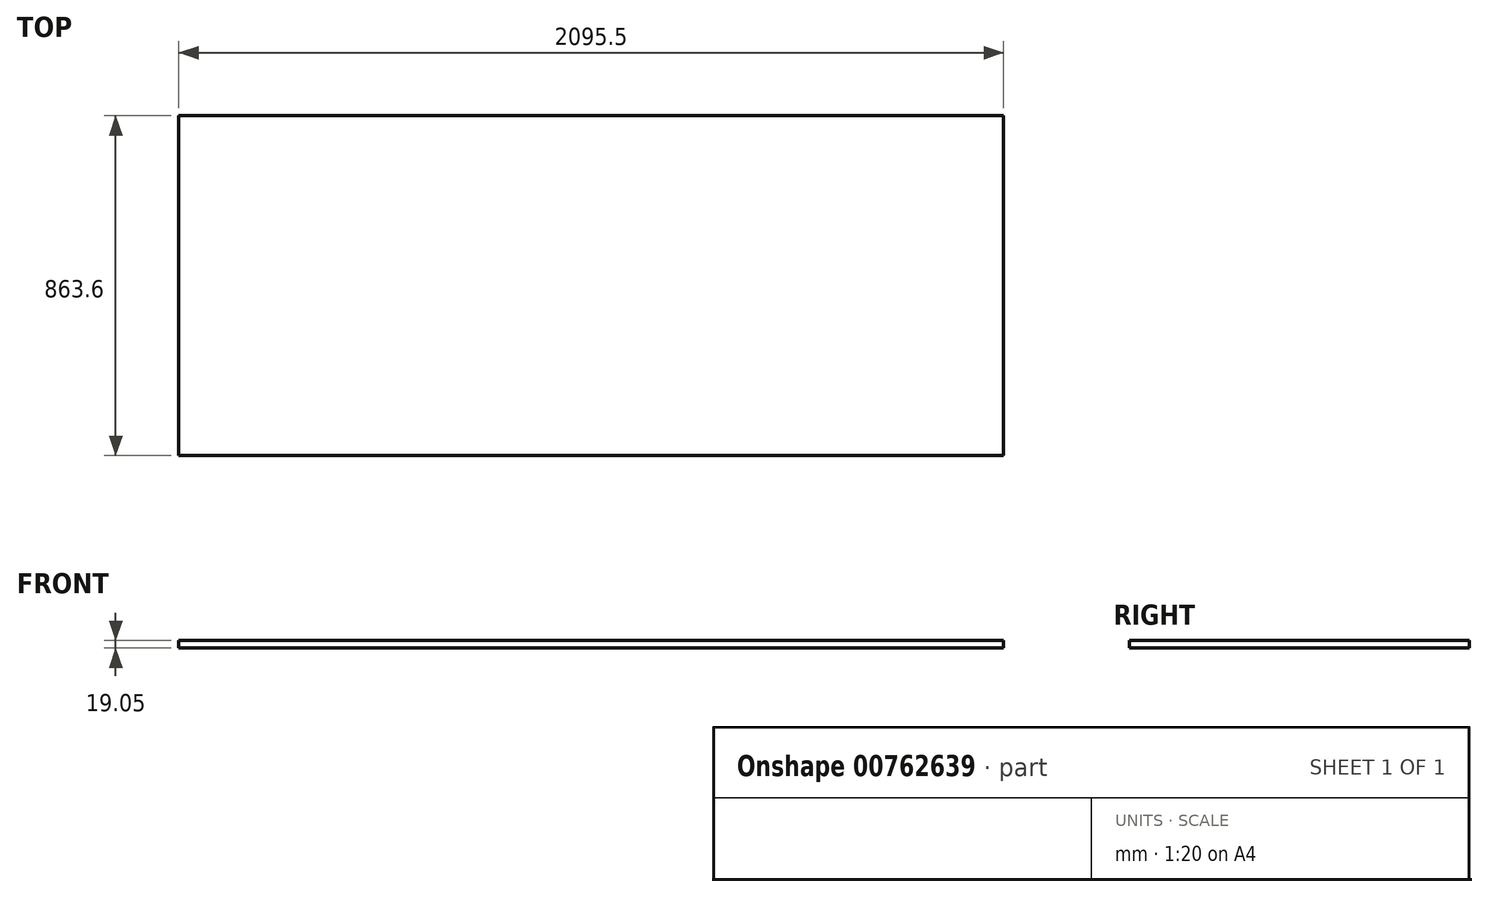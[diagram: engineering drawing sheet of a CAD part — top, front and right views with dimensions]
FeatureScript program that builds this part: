
annotation { "Feature Type Name" : "Feature", "Feature Type Description" : "" }
export const myFeature = defineFeature(function(context is Context, id is Id, definition is map)
    precondition{}
    {
        {
            var Q0;
            Q0=qCreatedBy(makeId("Top.planeOp"),FACE);
            var sketch = newSketch(context, id + "F0", { "sketchPlane" : qUnion([Q0])});
            skLineSegment(sketch, "E0.bottom", {"start": v(-1047.75, 431.8) * mm, "end": v(1047.75, 431.8) * mm});
            skLineSegment(sketch, "E0.top", {"start": v(-1047.75, -431.8) * mm, "end": v(1047.75, -431.8) * mm});
            skLineSegment(sketch, "E0.left", {"start": v(-1047.75, 431.8) * mm, "end": v(-1047.75, -431.8) * mm});
            skLineSegment(sketch, "E0.right", {"start": v(1047.75, 431.8) * mm, "end": v(1047.75, -431.8) * mm});
            skPoint(sketch, "E0.middle", {"position": v(0, 0) * mm});
            skSolve(sketch);
        }
        {
            var Q0;
            Q0=makeQuery(id+"F0.imprint","IMPRINT",FACE,{"disambiguationData":[TD([[makeQuery(id+"F0.imprint","IMPRINT",EDGE,{"derivedFrom":sQuery(id+"F0.wireOp",EDGE,"E0.bottom")}),-1.0]])]});
            extrude(context, id + "F1", {"entities" : qUnion([Q0]), "depth" : 19.05 * mm, "offsetDistance" : 25.4 * mm});
        }
    });
